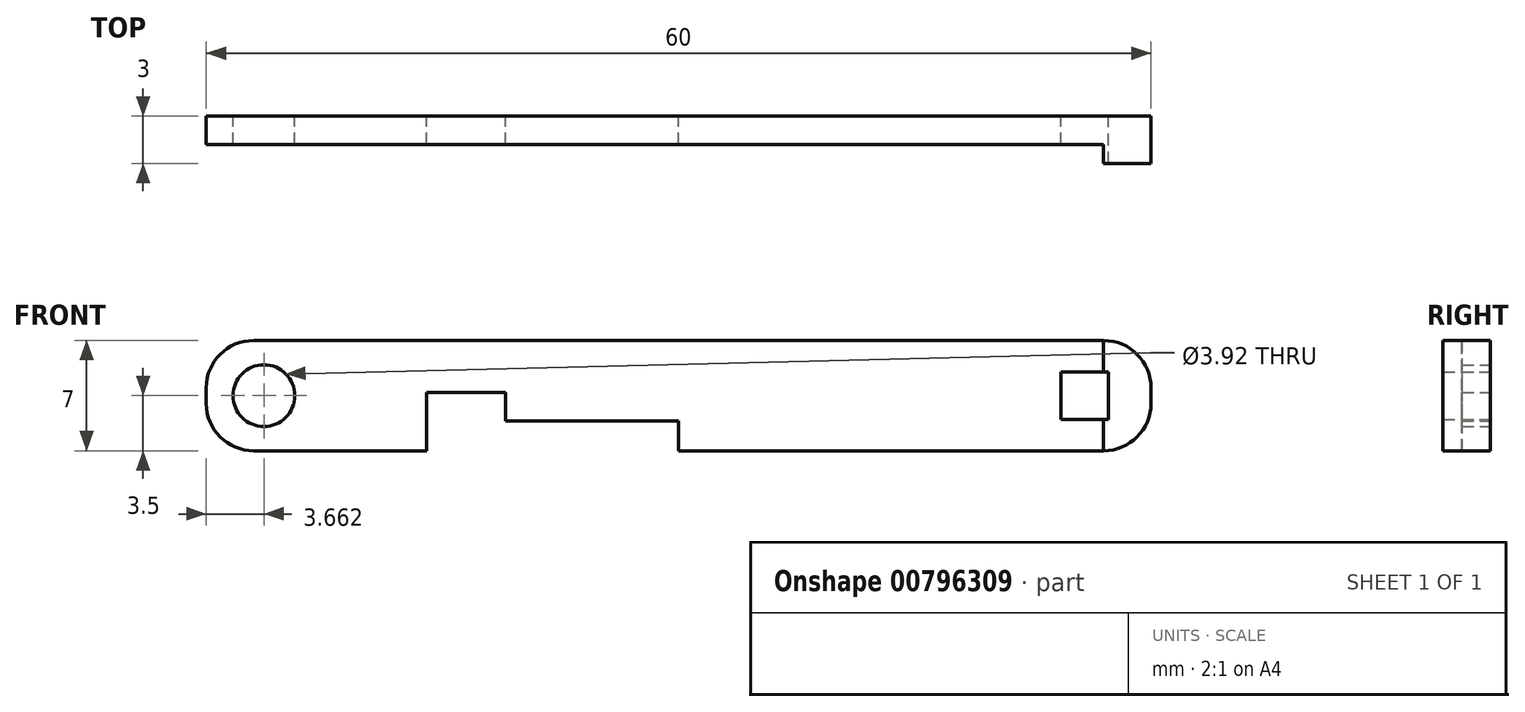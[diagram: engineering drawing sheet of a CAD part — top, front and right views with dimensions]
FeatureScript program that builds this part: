
annotation { "Feature Type Name" : "Feature", "Feature Type Description" : "" }
export const myFeature = defineFeature(function(context is Context, id is Id, definition is map)
    precondition{}
    {
        {
            var Q0;
            Q0=qCreatedBy(makeId("Front.planeOp"),FACE);
            var sketch = newSketch(context, id + "F0", { "sketchPlane" : qUnion([Q0])});
            skLineSegment(sketch, "E0.bottom", {"start": v(-27, 7) * mm, "end": v(27, 7) * mm});
            skLineSegment(sketch, "E0.top", {"start": v(-27, 0) * mm, "end": v(-16, 0) * mm});
            skLineSegment(sketch, "E0.left", {"start": v(-30, 4) * mm, "end": v(-30, 3) * mm});
            skLineSegment(sketch, "E0.right", {"start": v(30, 4) * mm, "end": v(30, 3) * mm});
            skLineSegment(sketch, "E1.bottom", {"start": v(24.3, 5) * mm, "end": v(27.3, 5) * mm});
            skLineSegment(sketch, "E1.top", {"start": v(24.3, 2) * mm, "end": v(27.3, 2) * mm});
            skLineSegment(sketch, "E1.left", {"start": v(24.3, 5) * mm, "end": v(24.3, 2) * mm});
            skLineSegment(sketch, "E1.right", {"start": v(27.3, 5) * mm, "end": v(27.3, 2) * mm});
            skPoint(sketch, "E2.visualSharp", {"position": v(30, 7) * mm});
            skArc(sketch, "E2.filletArc", {"start": v(30, 4) * mm, "mid": v(29.12, 6.12) * mm, "end": v(27, 7) * mm});
            skPoint(sketch, "E3.visualSharp", {"position": v(30, 0) * mm});
            skArc(sketch, "E3.filletArc", {"start": v(27, 0) * mm, "mid": v(29.12, 0.88) * mm, "end": v(30, 3) * mm});
            skPoint(sketch, "E4.visualSharp", {"position": v(-30, 7) * mm});
            skArc(sketch, "E4.filletArc", {"start": v(-27, 7) * mm, "mid": v(-29.12, 6.12) * mm, "end": v(-30, 4) * mm});
            skPoint(sketch, "E5.visualSharp", {"position": v(-30, 0) * mm});
            skArc(sketch, "E5.filletArc", {"start": v(-30, 3) * mm, "mid": v(-29.12, 0.88) * mm, "end": v(-27, 0) * mm});
            skCircle(sketch, "E6", {"center": v(-26.34, 3.5) * mm, "radius": 1.96 * mm});
            skLineSegment(sketch, "E7.top", {"start": v(-11, 1.9) * mm, "end": v(0, 1.9) * mm});
            skLineSegment(sketch, "E7.left", {"start": v(-16, 0) * mm, "end": v(-16, 1.9) * mm});
            skLineSegment(sketch, "E7.right", {"start": v(0, 0) * mm, "end": v(0, 1.9) * mm});
            skLineSegment(sketch, "E8.top", {"start": v(-16, 3.7) * mm, "end": v(-11, 3.7) * mm});
            skLineSegment(sketch, "E8.left", {"start": v(-16, 1.9) * mm, "end": v(-16, 3.7) * mm});
            skLineSegment(sketch, "E8.right", {"start": v(-11, 1.9) * mm, "end": v(-11, 3.7) * mm});
            skLineSegment(sketch, "E9.trimOffspring", {"start": v(0, 0) * mm, "end": v(27, 0) * mm});
            skSolve(sketch);
        }
        {
            var Q0;
            Q0=makeQuery(id+"F0.imprint","IMPRINT",FACE,{"disambiguationData":[TD([[makeQuery(id+"F0.imprint","IMPRINT",EDGE,{"derivedFrom":sQuery(id+"F0.wireOp",EDGE,"E0.bottom")}),-1.0]])]});
            extrude(context, id + "F1", {"entities" : qUnion([Q0]), "depth" : 1.8 * mm, "offsetDistance" : 25 * mm});
        }
        {
            var Q0;
            Q0=makeQuery(id+"F1.opExtrude","CAP_FACE",FACE,{"disambiguationData":[OSD([sQuery(id+"F0.wireOp",EDGE,"E0.bottom"),sQuery(id+"F0.wireOp",EDGE,"E0.top"),sQuery(id+"F0.wireOp",EDGE,"E0.left"),sQuery(id+"F0.wireOp",EDGE,"E0.right"),sQuery(id+"F0.wireOp",EDGE,"E1.bottom"),sQuery(id+"F0.wireOp",EDGE,"E1.top"),sQuery(id+"F0.wireOp",EDGE,"E1.left"),sQuery(id+"F0.wireOp",EDGE,"E1.right"),sQuery(id+"F0.wireOp",EDGE,"E2.filletArc"),sQuery(id+"F0.wireOp",EDGE,"E3.filletArc"),sQuery(id+"F0.wireOp",EDGE,"E4.filletArc"),sQuery(id+"F0.wireOp",EDGE,"E5.filletArc"),sQuery(id+"F0.wireOp",EDGE,"E6"),sQuery(id+"F0.wireOp",EDGE,"E7.top"),sQuery(id+"F0.wireOp",EDGE,"E7.left"),sQuery(id+"F0.wireOp",EDGE,"E7.right"),sQuery(id+"F0.wireOp",EDGE,"E8.top"),sQuery(id+"F0.wireOp",EDGE,"E8.left"),sQuery(id+"F0.wireOp",EDGE,"E8.right"),sQuery(id+"F0.wireOp",EDGE,"E9.trimOffspring")])],"isStart":false});
            var sketch = newSketch(context, id + "F2", { "sketchPlane" : qUnion([Q0])});
            skLineSegment(sketch, "E10.bottom", {"start": v(27, 0) * mm, "end": v(27, 0) * mm});
            skLineSegment(sketch, "E10.top", {"start": v(27, 7) * mm, "end": v(27, 7) * mm});
            skLineSegment(sketch, "E10.left", {"start": v(27, 0) * mm, "end": v(27, 2) * mm});
            skLineSegment(sketch, "E10.right", {"start": v(30, 3) * mm, "end": v(30, 4) * mm});
            skPoint(sketch, "E11.visualSharp", {"position": v(30, 7) * mm});
            skArc(sketch, "E11.filletArc", {"start": v(30, 4) * mm, "mid": v(29.12, 6.12) * mm, "end": v(27, 7) * mm});
            skPoint(sketch, "E12.visualSharp", {"position": v(30, 0) * mm});
            skArc(sketch, "E12.filletArc", {"start": v(27, 0) * mm, "mid": v(29.12, 0.88) * mm, "end": v(30, 3) * mm});
            skLineSegment(sketch, "E13", {"start": v(27.3, 2) * mm, "end": v(27, 2) * mm});
            skLineSegment(sketch, "E14", {"start": v(27.3, 5) * mm, "end": v(27, 5) * mm});
            skLineSegment(sketch, "E15.trimOffspring", {"start": v(27, 5) * mm, "end": v(27, 7) * mm});
            skLineSegment(sketch, "E16", {"start": v(27.3, 5) * mm, "end": v(27.3, 2) * mm});
            skSolve(sketch);
        }
        {
            var Q0;
            Q0 = qSketchRegion(id + "F2", true);
            extrude(context, id + "F3", {"entities" : qUnion([Q0]), "operationType" : NewBodyOperationType.ADD, "depth" : 1.2 * mm, "offsetDistance" : 25 * mm});
        }
    });
